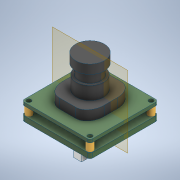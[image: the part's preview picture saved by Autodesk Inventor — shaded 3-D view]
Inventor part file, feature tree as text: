
AUTODESK INVENTOR PART (.ipt)
format: ipt  version: 2022.2 (Build 262287000, 287)  size: 252,416 bytes
history: native  units: in
note: dims shown in document units (in); Inventor stores cm internally (conversion verified against a paired STEP export)
features: extrude x1, sketch x1, other x1
ambient origin geometry x8: Origin, YZ Plane, XZ Plane, XY Plane, X Axis, Y Axis, Z Axis, Center Point
bodies: Solid1 (feature_tree)
feature tree (3):
  extrude  "Extrusion1"  Depth=0.0394in TaperAngle=0.0deg
  sketch  "Sketch1"  dims[d0=0.0591in d1=0.0394in d2=0.0in]
  other  "Part 1"
